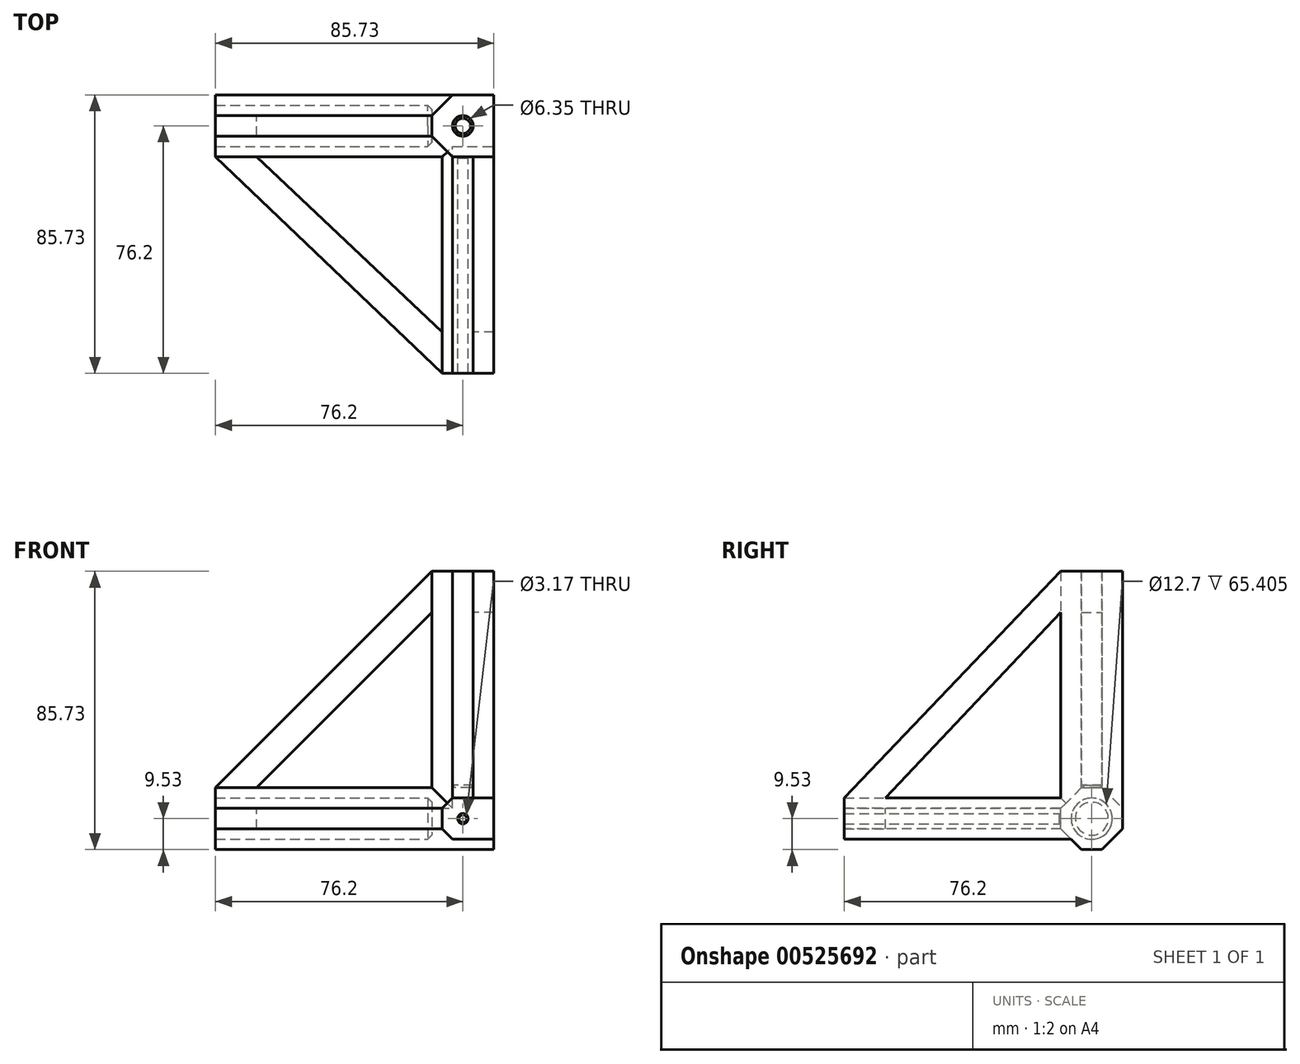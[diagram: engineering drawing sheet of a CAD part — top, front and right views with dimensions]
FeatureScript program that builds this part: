
annotation { "Feature Type Name" : "Feature", "Feature Type Description" : "" }
export const myFeature = defineFeature(function(context is Context, id is Id, definition is map)
    precondition{}
    {
        {
            var Q0;
            Q0=qCreatedBy(makeId("Top.planeOp"),FACE);
            var sketch = newSketch(context, id + "F0", { "sketchPlane" : qUnion([Q0])});
            skCircle(sketch, "E0", {"center": v(0, 0) * mm, "radius": 3.18 * mm});
            skLineSegment(sketch, "E1.bottom", {"start": v(9.53, -9.52) * mm, "end": v(-9.53, -9.53) * mm});
            skLineSegment(sketch, "E1.top", {"start": v(9.52, 9.53) * mm, "end": v(-9.53, 9.52) * mm});
            skLineSegment(sketch, "E1.left", {"start": v(9.53, -9.52) * mm, "end": v(9.52, 9.53) * mm});
            skLineSegment(sketch, "E1.right", {"start": v(-9.53, -9.53) * mm, "end": v(-9.53, 9.52) * mm});
            skSolve(sketch);
        }
        {
            var Q0;
            Q0 = qSketchRegion(id + "F0", true);
            extrude(context, id + "F1", {"entities" : qUnion([Q0]), "depth" : 76.2 * mm, "offsetDistance" : 25.4 * mm});
        }
        {
            var Q0;
            Q0=qCreatedBy(makeId("Front.planeOp"),FACE);
            var sketch = newSketch(context, id + "F2", { "sketchPlane" : qUnion([Q0])});
            skCircle(sketch, "E2", {"center": v(0, 0) * mm, "radius": 1.59 * mm});
            skLineSegment(sketch, "E3.bottom", {"start": v(9.53, 6.35) * mm, "end": v(-6.35, 6.35) * mm});
            skLineSegment(sketch, "E3.top", {"start": v(9.53, -6.35) * mm, "end": v(-6.35, -6.35) * mm});
            skLineSegment(sketch, "E3.left", {"start": v(9.53, 6.35) * mm, "end": v(9.53, -6.35) * mm});
            skLineSegment(sketch, "E3.right", {"start": v(-6.35, 6.35) * mm, "end": v(-6.35, -6.35) * mm});
            skSolve(sketch);
        }
        {
            var Q0;
            Q0 = qSketchRegion(id + "F2", true);
            extrude(context, id + "F3", {"entities" : qUnion([Q0]), "operationType" : NewBodyOperationType.ADD, "depth" : 76.2 * mm, "offsetDistance" : 25.4 * mm});
        }
        {
            var Q0;
            Q0=qCreatedBy(makeId("Right.planeOp"),FACE);
            var sketch = newSketch(context, id + "F4", { "sketchPlane" : qUnion([Q0])});
            skCircle(sketch, "E4", {"center": v(0, 0) * mm, "radius": 6.35 * mm});
            skLineSegment(sketch, "E5.bottom", {"start": v(9.53, -9.52) * mm, "end": v(-9.53, -9.53) * mm});
            skLineSegment(sketch, "E5.top", {"start": v(9.53, 9.53) * mm, "end": v(-9.53, 9.52) * mm});
            skLineSegment(sketch, "E5.left", {"start": v(9.53, -9.52) * mm, "end": v(9.53, 9.53) * mm});
            skLineSegment(sketch, "E5.right", {"start": v(-9.53, -9.53) * mm, "end": v(-9.53, 9.52) * mm});
            skSolve(sketch);
        }
        {
            var Q0;
            Q0 = qSketchRegion(id + "F4", true);
            extrude(context, id + "F5", {"entities" : qUnion([Q0]), "operationType" : NewBodyOperationType.ADD, "oppositeDirection" : true, "depth" : 76.2 * mm, "offsetDistance" : 25.4 * mm});
        }
        {
            var Q0;
            Q0=qCreatedBy(makeId("Front.planeOp"),FACE);
            var sketch = newSketch(context, id + "F6", { "sketchPlane" : qUnion([Q0])});
            skLineSegment(sketch, "E6.bottom", {"start": v(9.53, 9.53) * mm, "end": v(-9.53, 9.53) * mm});
            skLineSegment(sketch, "E6.top", {"start": v(9.53, -9.53) * mm, "end": v(-9.53, -9.53) * mm});
            skLineSegment(sketch, "E6.left", {"start": v(9.53, 9.53) * mm, "end": v(9.53, -9.52) * mm});
            skLineSegment(sketch, "E6.right", {"start": v(-9.53, 9.53) * mm, "end": v(-9.53, -9.53) * mm});
            skSolve(sketch);
        }
        {
            var Q0;
            Q0 = qSketchRegion(id + "F6", true);
            extrude(context, id + "F7", {"entities" : qUnion([Q0]), "operationType" : NewBodyOperationType.ADD, "depth" : 19.05 * mm, "offsetDistance" : 25.4 * mm, "symmetric" : true});
        }
        {
            var Q0;
            {var subQ0=sQuery(id+"F2.wireOp",EDGE,"E3.right");var subQ2=sQuery(id+"F2.wireOp",EDGE,"E3.bottom");Q0=makeQuery(id+"F5.boolean.opBoolean","SPLIT",FACE,{"disambiguationData":[TD([makeQuery(id+"F3.opExtrude","SWEPT_FACE",FACE,{"disambiguationData":[OSD([subQ2])]})])],"derivedFrom":makeQuery(id+"F3.opExtrude","SWEPT_FACE",FACE,{"disambiguationData":[OSD([subQ0])]})});}
            var sketch = newSketch(context, id + "F8", { "sketchPlane" : qUnion([Q0])});
            skLineSegment(sketch, "E7.bottom", {"start": v(76.2, -3.18) * mm, "end": v(63.5, -3.18) * mm});
            skLineSegment(sketch, "E7.top", {"start": v(76.2, 3.18) * mm, "end": v(63.5, 3.17) * mm});
            skLineSegment(sketch, "E7.left", {"start": v(76.2, -3.18) * mm, "end": v(76.2, 3.18) * mm});
            skLineSegment(sketch, "E7.right", {"start": v(63.5, -3.18) * mm, "end": v(63.5, 3.17) * mm});
            skSolve(sketch);
        }
        {
            var Q0;
            {var subQ0=sQuery(id+"F4.wireOp",EDGE,"E5.right");Q0=makeQuery(id+"F7.boolean.opBoolean","MERGE",FACE,{"derivedFrom":[makeQuery(id+"F5.boolean.opBoolean","SPLIT",FACE,{"disambiguationData":[TD([makeQuery(id+"F3.opExtrude","SWEPT_FACE",FACE,{"disambiguationData":[OSD([sQuery(id+"F2.wireOp",EDGE,"E3.bottom")])]})])],"derivedFrom":makeQuery(id+"F5.opExtrude","SWEPT_FACE",FACE,{"disambiguationData":[OSD([subQ0])]})}),makeQuery(id+"F7.opExtrude","CAP_FACE",FACE,{"disambiguationData":[OSD([sQuery(id+"F6.wireOp",EDGE,"E6.bottom"),sQuery(id+"F6.wireOp",EDGE,"E6.top"),sQuery(id+"F6.wireOp",EDGE,"E6.left"),sQuery(id+"F6.wireOp",EDGE,"E6.right")])],"isStart":false})]});}
            var sketch = newSketch(context, id + "F9", { "sketchPlane" : qUnion([Q0])});
            skLineSegment(sketch, "E8.bottom", {"start": v(-76.2, -3.18) * mm, "end": v(-63.5, -3.17) * mm});
            skLineSegment(sketch, "E8.top", {"start": v(-76.2, 3.18) * mm, "end": v(-63.5, 3.18) * mm});
            skLineSegment(sketch, "E8.left", {"start": v(-76.2, -3.18) * mm, "end": v(-76.2, 3.18) * mm});
            skLineSegment(sketch, "E8.right", {"start": v(-63.5, -3.17) * mm, "end": v(-63.5, 3.18) * mm});
            skSolve(sketch);
        }
        {
            var Q1;
            Q1=makeQuery(id+"F9.imprint","IMPRINT",FACE,{"disambiguationData":[TD([[makeQuery(id+"F9.imprint","IMPRINT",EDGE,{"derivedFrom":sQuery(id+"F9.wireOp",EDGE,"E8.bottom")}),1.0]])]});
            var Q2;
            Q2=makeQuery(id+"F8.imprint","IMPRINT",FACE,{"disambiguationData":[TD([[makeQuery(id+"F8.imprint","IMPRINT",EDGE,{"derivedFrom":sQuery(id+"F8.wireOp",EDGE,"E7.bottom")}),-1.0]])]});
            loft(context, id + "F10", {"operationType" : NewBodyOperationType.ADD, "sheetProfilesArray" : [{ "sheetProfileEntities" : qUnion([Q1]) }, { "sheetProfileEntities" : qUnion([Q2]) }]});
        }
        {
            var Q0;
            Q0=makeQuery(id+"F3.opExtrude","SWEPT_EDGE",EDGE,{"disambiguationData":[OSD([sQuery(id+"F2.wireOp",EDGE,"E3.bottom"),sQuery(id+"F2.wireOp",EDGE,"E3.right")])]});
            var Q1;
            Q1=makeQuery(id+"F3.opExtrude","SWEPT_EDGE",EDGE,{"disambiguationData":[OSD([sQuery(id+"F2.wireOp",EDGE,"E3.top"),sQuery(id+"F2.wireOp",EDGE,"E3.right")])]});
            chamfer(context, id + "F11", {"entities" : qUnion([Q0, Q1]), "width" : 3.17 * mm, "tangentPropagation" : true});
        }
        {
            var Q0;
            {var subQ0=sQuery(id+"F0.wireOp",EDGE,"E1.right");var subQ2=sQuery(id+"F0.wireOp",EDGE,"E1.bottom");Q0=makeQuery(id+"F5.boolean.opBoolean","SPLIT",FACE,{"disambiguationData":[TD([makeQuery(id+"F1.opExtrude","SWEPT_FACE",FACE,{"disambiguationData":[OSD([subQ2])]})])],"derivedFrom":makeQuery(id+"F1.opExtrude","SWEPT_FACE",FACE,{"disambiguationData":[OSD([subQ0])]})});}
            var sketch = newSketch(context, id + "F12", { "sketchPlane" : qUnion([Q0])});
            skLineSegment(sketch, "E9.bottom", {"start": v(3.17, 76.2) * mm, "end": v(-3.18, 76.2) * mm});
            skLineSegment(sketch, "E9.top", {"start": v(3.18, 63.5) * mm, "end": v(-3.17, 63.5) * mm});
            skLineSegment(sketch, "E9.left", {"start": v(3.17, 76.2) * mm, "end": v(3.18, 63.5) * mm});
            skLineSegment(sketch, "E9.right", {"start": v(-3.18, 76.2) * mm, "end": v(-3.17, 63.5) * mm});
            skSolve(sketch);
        }
        {
            var Q0;
            {var subQ2=sQuery(id+"F4.wireOp",EDGE,"E5.top");Q0=makeQuery(id+"F7.boolean.opBoolean","MERGE",FACE,{"derivedFrom":[makeQuery(id+"F5.boolean.opBoolean","SPLIT",FACE,{"disambiguationData":[TD([makeQuery(id+"F1.opExtrude","SWEPT_FACE",FACE,{"disambiguationData":[OSD([sQuery(id+"F0.wireOp",EDGE,"E1.bottom")])]})])],"derivedFrom":makeQuery(id+"F5.opExtrude","SWEPT_FACE",FACE,{"disambiguationData":[OSD([subQ2])]})}),makeQuery(id+"F7.opExtrude","SWEPT_FACE",FACE,{"disambiguationData":[OSD([sQuery(id+"F6.wireOp",EDGE,"E6.bottom")])]})]});}
            var sketch = newSketch(context, id + "F13", { "sketchPlane" : qUnion([Q0])});
            skLineSegment(sketch, "E10.bottom", {"start": v(-76.2, -3.17) * mm, "end": v(-63.5, -3.17) * mm});
            skLineSegment(sketch, "E10.top", {"start": v(-76.2, 3.18) * mm, "end": v(-63.5, 3.18) * mm});
            skLineSegment(sketch, "E10.left", {"start": v(-76.2, -3.17) * mm, "end": v(-76.2, 3.18) * mm});
            skLineSegment(sketch, "E10.right", {"start": v(-63.5, -3.17) * mm, "end": v(-63.5, 3.18) * mm});
            skSolve(sketch);
        }
        {
            var Q1;
            Q1=makeQuery(id+"F13.imprint","IMPRINT",FACE,{"disambiguationData":[TD([[makeQuery(id+"F13.imprint","IMPRINT",EDGE,{"derivedFrom":sQuery(id+"F13.wireOp",EDGE,"E10.bottom")}),1.0]])]});
            var Q2;
            Q2=makeQuery(id+"F12.imprint","IMPRINT",FACE,{"disambiguationData":[TD([[makeQuery(id+"F12.imprint","IMPRINT",EDGE,{"derivedFrom":sQuery(id+"F12.wireOp",EDGE,"E9.bottom")}),1.0]])]});
            loft(context, id + "F14", {"operationType" : NewBodyOperationType.ADD, "sheetProfilesArray" : [{ "sheetProfileEntities" : qUnion([Q1]) }, { "sheetProfileEntities" : qUnion([Q2]) }]});
        }
        {
            var Q0;
            Q0=makeQuery(id+"F1.opExtrude","SWEPT_EDGE",EDGE,{"disambiguationData":[OSD([sQuery(id+"F0.wireOp",EDGE,"E1.top"),sQuery(id+"F0.wireOp",EDGE,"E1.right")])]});
            var Q1;
            Q1=makeQuery(id+"F1.opExtrude","SWEPT_EDGE",EDGE,{"disambiguationData":[OSD([sQuery(id+"F0.wireOp",EDGE,"E1.bottom"),sQuery(id+"F0.wireOp",EDGE,"E1.right")])]});
            chamfer(context, id + "F15", {"entities" : qUnion([Q0, Q1]), "width" : 6.35 * mm, "tangentPropagation" : true});
        }
        {
            var Q0;
            {var subQ2=sQuery(id+"F2.wireOp",EDGE,"E3.bottom");Q0=makeQuery(id+"F3.boolean.opBoolean","SPLIT",FACE,{"disambiguationData":[TD([makeQuery(id+"F1.opExtrude","SWEPT_FACE",FACE,{"disambiguationData":[OSD([sQuery(id+"F0.wireOp",EDGE,"E1.bottom")])]})])],"derivedFrom":makeQuery(id+"F3.opExtrude","SWEPT_FACE",FACE,{"disambiguationData":[OSD([subQ2])]})});}
            var sketch = newSketch(context, id + "F16", { "sketchPlane" : qUnion([Q0])});
            skLineSegment(sketch, "E11.bottom", {"start": v(9.53, -76.2) * mm, "end": v(3.17, -76.2) * mm});
            skLineSegment(sketch, "E11.top", {"start": v(9.52, -63.5) * mm, "end": v(3.17, -63.5) * mm});
            skLineSegment(sketch, "E11.left", {"start": v(9.53, -76.2) * mm, "end": v(9.53, -63.5) * mm});
            skLineSegment(sketch, "E11.right", {"start": v(3.17, -76.2) * mm, "end": v(3.17, -63.5) * mm});
            skSolve(sketch);
        }
        {
            var Q0;
            {var subQ0=sQuery(id+"F0.wireOp",EDGE,"E1.left");var subQ3=sQuery(id+"F0.wireOp",EDGE,"E1.bottom");Q0=makeQuery(id+"F3.boolean.opBoolean","SPLIT",FACE,{"disambiguationData":[TD([makeQuery(id+"F1.opExtrude","SWEPT_FACE",FACE,{"disambiguationData":[OSD([subQ0])]})])],"derivedFrom":makeQuery(id+"F1.opExtrude","SWEPT_FACE",FACE,{"disambiguationData":[OSD([subQ3])]})});}
            var sketch = newSketch(context, id + "F17", { "sketchPlane" : qUnion([Q0])});
            skLineSegment(sketch, "E12.bottom", {"start": v(9.52, 76.2) * mm, "end": v(3.17, 76.2) * mm});
            skLineSegment(sketch, "E12.top", {"start": v(9.52, 63.5) * mm, "end": v(3.18, 63.5) * mm});
            skLineSegment(sketch, "E12.left", {"start": v(9.52, 76.2) * mm, "end": v(9.52, 63.5) * mm});
            skLineSegment(sketch, "E12.right", {"start": v(3.17, 76.2) * mm, "end": v(3.18, 63.5) * mm});
            skSolve(sketch);
        }
        {
            var Q1;
            Q1=makeQuery(id+"F16.imprint","IMPRINT",FACE,{"disambiguationData":[TD([[makeQuery(id+"F16.imprint","IMPRINT",EDGE,{"derivedFrom":sQuery(id+"F16.wireOp",EDGE,"E11.bottom")}),-1.0]])]});
            var Q2;
            Q2=makeQuery(id+"F17.imprint","IMPRINT",FACE,{"disambiguationData":[TD([[makeQuery(id+"F17.imprint","IMPRINT",EDGE,{"derivedFrom":sQuery(id+"F17.wireOp",EDGE,"E12.bottom")}),1.0]])]});
            loft(context, id + "F18", {"operationType" : NewBodyOperationType.ADD, "sheetProfilesArray" : [{ "sheetProfileEntities" : qUnion([Q1]) }, { "sheetProfileEntities" : qUnion([Q2]) }]});
        }
        {
            var Q0;
            Q0=makeQuery(id+"F7.boolean.opBoolean","MERGE",EDGE,{"derivedFrom":[makeQuery(id+"F5.opExtrude","SWEPT_EDGE",EDGE,{"disambiguationData":[OSD([sQuery(id+"F4.wireOp",EDGE,"E5.bottom"),sQuery(id+"F4.wireOp",EDGE,"E5.right")])]}),makeQuery(id+"F7.opExtrude","CAP_EDGE",EDGE,{"disambiguationData":[OSD([sQuery(id+"F6.wireOp",EDGE,"E6.top")])],"isStart":false})]});
            chamfer(context, id + "F19", {"entities" : qUnion([Q0]), "width" : 6.35 * mm, "tangentPropagation" : true});
        }
        {
            var Q0;
            Q0=makeQuery(id+"F7.boolean.opBoolean","MERGE",EDGE,{"derivedFrom":[makeQuery(id+"F5.opExtrude","SWEPT_EDGE",EDGE,{"disambiguationData":[OSD([sQuery(id+"F4.wireOp",EDGE,"E5.bottom"),sQuery(id+"F4.wireOp",EDGE,"E5.left")])]}),makeQuery(id+"F7.opExtrude","CAP_EDGE",EDGE,{"disambiguationData":[OSD([sQuery(id+"F6.wireOp",EDGE,"E6.top")])],"isStart":true})]});
            chamfer(context, id + "F20", {"entities" : qUnion([Q0]), "width" : 6.35 * mm, "tangentPropagation" : true});
        }
        {
            var Q0;
            {var subQ2=sQuery(id+"F0.wireOp",EDGE,"E1.right");var subQ7=sQuery(id+"F4.wireOp",EDGE,"E4");Q0=makeQuery(id+"F7.boolean.opBoolean","INTERSECT",EDGE,{"derivedFrom":[makeQuery(id+"F5.boolean.opBoolean","SPLIT",FACE,{"disambiguationData":[TD([makeQuery(id+"F1.opExtrude","SWEPT_FACE",FACE,{"disambiguationData":[OSD([subQ2])]})])],"derivedFrom":makeQuery(id+"F5.opExtrude","SWEPT_FACE",FACE,{"disambiguationData":[OSD([subQ7])]})}),makeQuery(id+"F7.opExtrude","SWEPT_FACE",FACE,{"disambiguationData":[OSD([sQuery(id+"F6.wireOp",EDGE,"E6.right")])]})]});}
            chamfer(context, id + "F21", {"entities" : qUnion([Q0]), "width" : 1.27 * mm, "tangentPropagation" : true});
        }
        {
            var Q0;
            {var subQ4=sQuery(id+"F0.wireOp",EDGE,"E0");var subQ5=sQuery(id+"F2.wireOp",EDGE,"E3.bottom");Q0=makeQuery(id+"F7.boolean.opBoolean","INTERSECT",EDGE,{"derivedFrom":[makeQuery(id+"F3.boolean.opBoolean","SPLIT",FACE,{"disambiguationData":[TD([makeQuery(id+"F3.opExtrude","SWEPT_FACE",FACE,{"disambiguationData":[OSD([subQ5])]})])],"derivedFrom":makeQuery(id+"F1.opExtrude","SWEPT_FACE",FACE,{"disambiguationData":[OSD([subQ4])]})}),makeQuery(id+"F7.opExtrude","SWEPT_FACE",FACE,{"disambiguationData":[OSD([sQuery(id+"F6.wireOp",EDGE,"E6.bottom")])]})]});}
            chamfer(context, id + "F22", {"entities" : qUnion([Q0]), "width" : 0.8 * mm, "tangentPropagation" : true});
        }
        {
            var Q0;
            Q0=makeQuery(id+"F7.boolean.opBoolean","INTERSECT",EDGE,{"derivedFrom":[makeQuery(id+"F3.opExtrude","SWEPT_FACE",FACE,{"disambiguationData":[OSD([sQuery(id+"F2.wireOp",EDGE,"E2")])]}),makeQuery(id+"F7.opExtrude","CAP_FACE",FACE,{"disambiguationData":[OSD([sQuery(id+"F6.wireOp",EDGE,"E6.bottom"),sQuery(id+"F6.wireOp",EDGE,"E6.top"),sQuery(id+"F6.wireOp",EDGE,"E6.left"),sQuery(id+"F6.wireOp",EDGE,"E6.right")])],"isStart":false})]});
            chamfer(context, id + "F23", {"entities" : qUnion([Q0]), "width" : 0.4 * mm, "tangentPropagation" : true});
        }
        {
            var Q0;
            Q0=makeQuery(id+"F5.opExtrude","SWEPT_EDGE",EDGE,{"disambiguationData":[OSD([sQuery(id+"F4.wireOp",EDGE,"E5.top"),sQuery(id+"F4.wireOp",EDGE,"E5.right")])]});
            var Q1;
            Q1=makeQuery(id+"F5.opExtrude","SWEPT_EDGE",EDGE,{"disambiguationData":[OSD([sQuery(id+"F4.wireOp",EDGE,"E5.top"),sQuery(id+"F4.wireOp",EDGE,"E5.left")])]});
            chamfer(context, id + "F24", {"entities" : qUnion([Q0, Q1]), "width" : 6.35 * mm, "tangentPropagation" : true});
        }
    });
